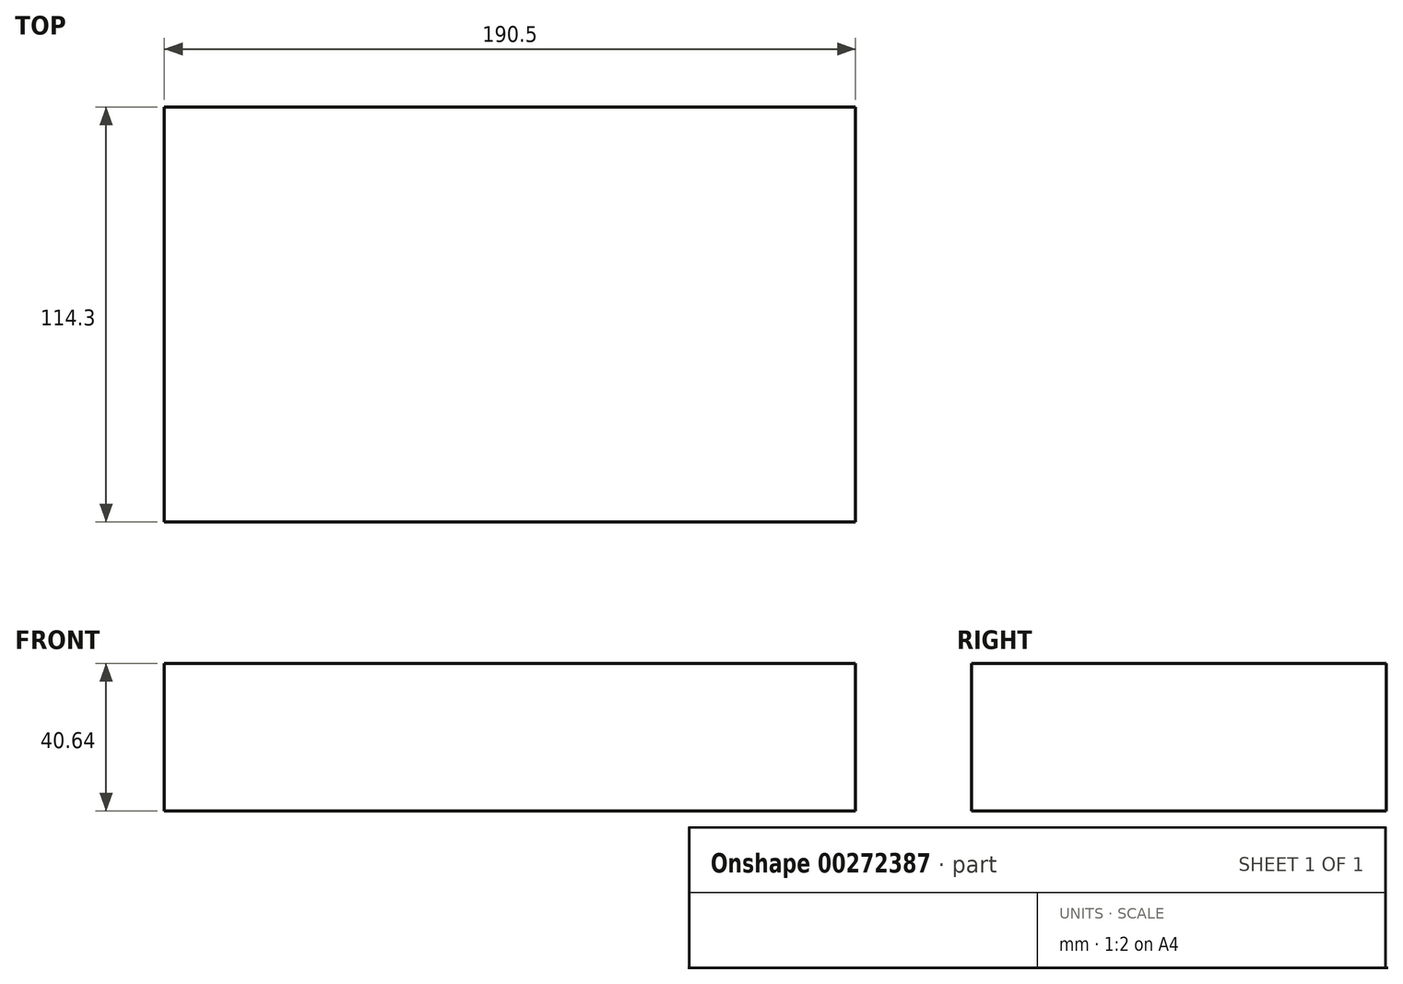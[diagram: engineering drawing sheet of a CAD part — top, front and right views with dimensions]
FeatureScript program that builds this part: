
annotation { "Feature Type Name" : "Feature", "Feature Type Description" : "" }
export const myFeature = defineFeature(function(context is Context, id is Id, definition is map)
    precondition{}
    {
        {
            var Q0;
            Q0=qCreatedBy(makeId("Top.planeOp"),FACE);
            var sketch = newSketch(context, id + "F0", { "sketchPlane" : qUnion([Q0])});
            skLineSegment(sketch, "E0.bottom", {"start": v(-110.82, -74.46) * mm, "end": v(79.68, -74.46) * mm});
            skLineSegment(sketch, "E0.top", {"start": v(-110.82, 39.84) * mm, "end": v(79.68, 39.84) * mm});
            skLineSegment(sketch, "E0.left", {"start": v(-110.82, -74.46) * mm, "end": v(-110.82, 39.84) * mm});
            skLineSegment(sketch, "E0.right", {"start": v(79.68, -74.46) * mm, "end": v(79.68, 39.84) * mm});
            skSolve(sketch);
        }
        {
            var Q0;
            Q0=makeQuery(id+"F0.imprint","IMPRINT",FACE,{"disambiguationData":[TD([[makeQuery(id+"F0.imprint","IMPRINT",EDGE,{"derivedFrom":sQuery(id+"F0.wireOp",EDGE,"E0.bottom")}),1.0]])]});
            extrude(context, id + "F1", {"entities" : qUnion([Q0]), "depth" : 40.64 * mm});
        }
    });
